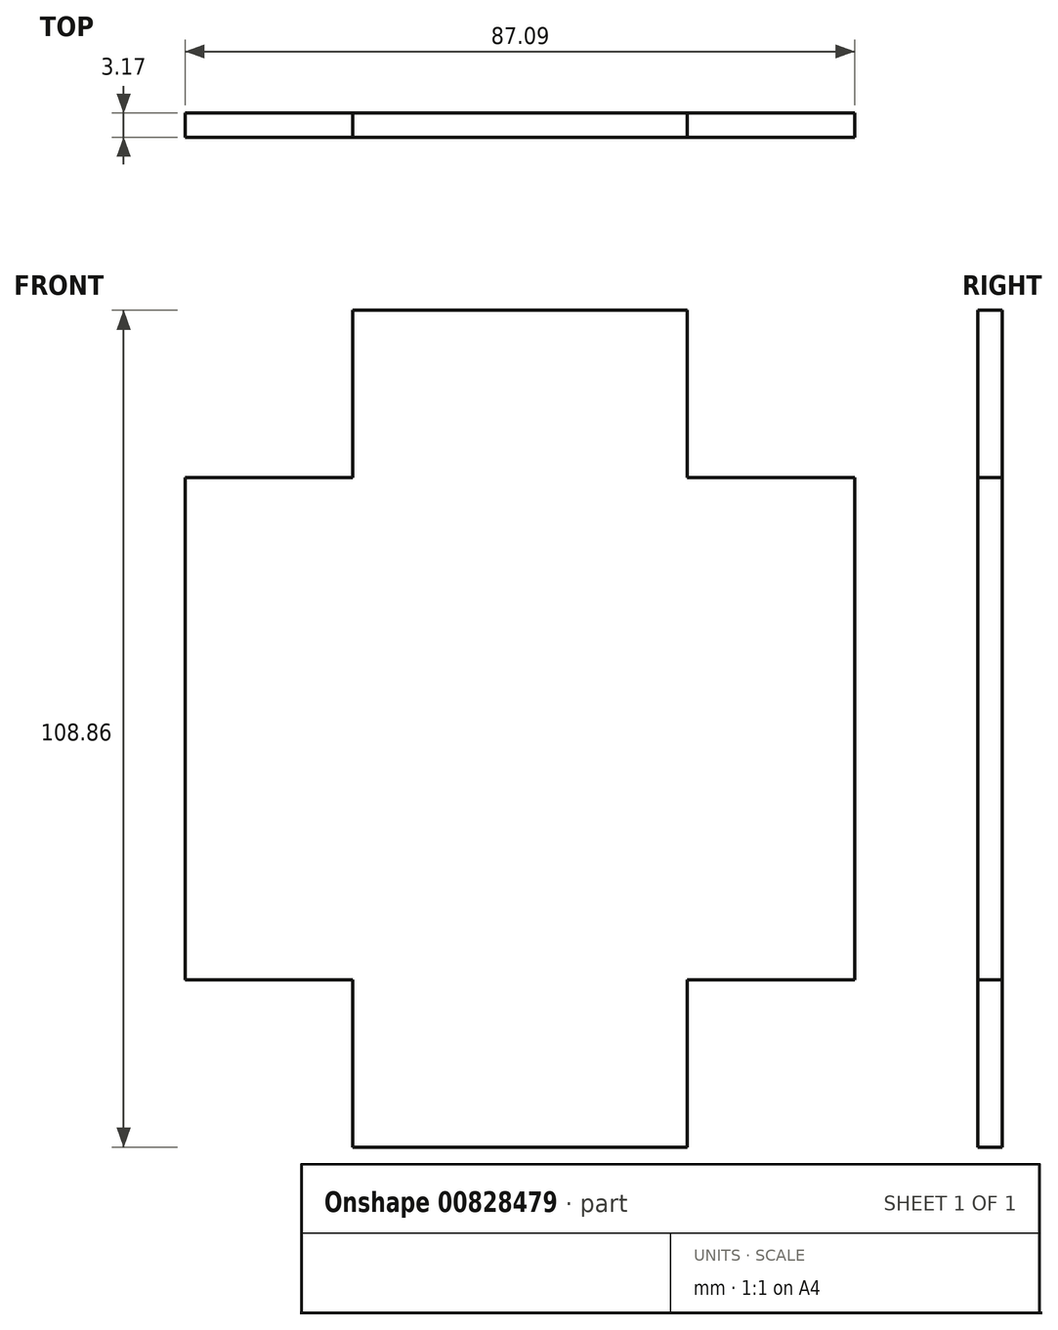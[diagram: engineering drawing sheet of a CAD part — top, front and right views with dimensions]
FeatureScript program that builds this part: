
annotation { "Feature Type Name" : "Feature", "Feature Type Description" : "" }
export const myFeature = defineFeature(function(context is Context, id is Id, definition is map)
    precondition{}
    {
        {
            var Q0;
            Q0=qCreatedBy(makeId("Front.planeOp"),FACE);
            var sketch = newSketch(context, id + "F0", { "sketchPlane" : qUnion([Q0])});
            skLineSegment(sketch, "E0", {"start": v(0, 0) * mm, "end": v(0, 65.31) * mm});
            skLineSegment(sketch, "E1", {"start": v(0, 65.31) * mm, "end": v(21.77, 65.31) * mm});
            skLineSegment(sketch, "E2", {"start": v(21.77, 65.31) * mm, "end": v(21.77, 87.09) * mm});
            skLineSegment(sketch, "E3", {"start": v(21.77, 87.09) * mm, "end": v(65.31, 87.09) * mm});
            skLineSegment(sketch, "E4", {"start": v(65.31, 87.09) * mm, "end": v(65.31, 65.31) * mm});
            skLineSegment(sketch, "E5", {"start": v(65.31, 65.31) * mm, "end": v(87.09, 65.31) * mm});
            skLineSegment(sketch, "E6", {"start": v(87.09, 65.31) * mm, "end": v(87.09, 0) * mm});
            skLineSegment(sketch, "E7", {"start": v(87.09, 0) * mm, "end": v(65.31, 0) * mm});
            skLineSegment(sketch, "E8", {"start": v(65.31, 0) * mm, "end": v(65.31, -21.77) * mm});
            skLineSegment(sketch, "E9", {"start": v(65.31, -21.77) * mm, "end": v(21.77, -21.77) * mm});
            skLineSegment(sketch, "E10", {"start": v(21.77, -21.77) * mm, "end": v(21.77, 0) * mm});
            skLineSegment(sketch, "E11", {"start": v(21.77, 0) * mm, "end": v(0, 0) * mm});
            skSolve(sketch);
        }
        {
            var Q0;
            Q0 = qSketchRegion(id + "F0", true);
            extrude(context, id + "F1", {"entities" : qUnion([Q0]), "depth" : 3.17 * mm, "offsetDistance" : 25.4 * mm});
        }
    });
